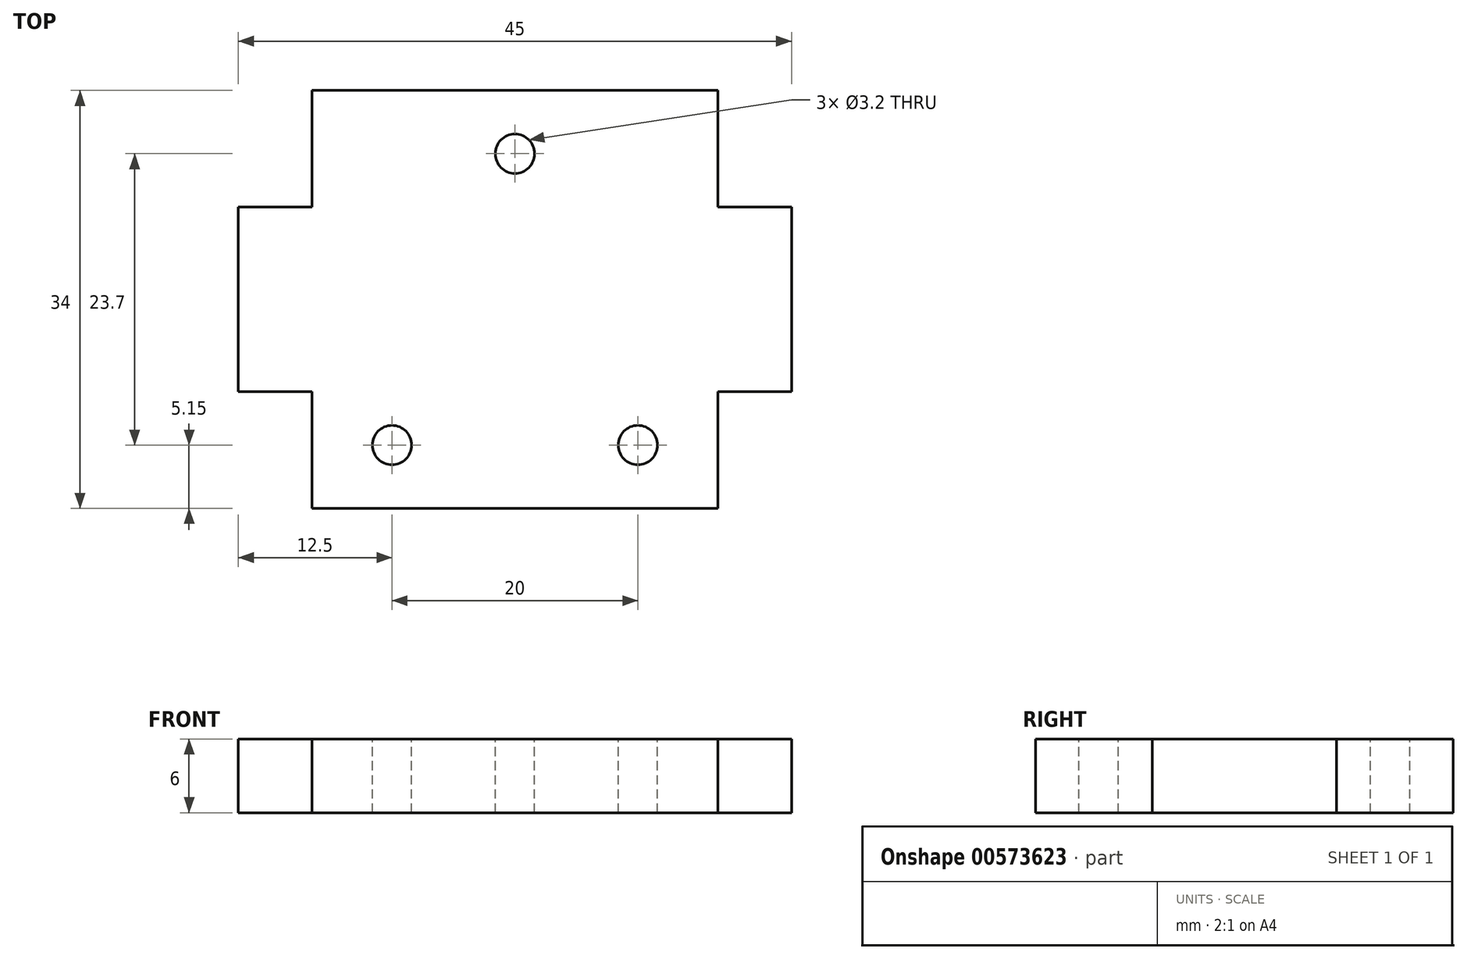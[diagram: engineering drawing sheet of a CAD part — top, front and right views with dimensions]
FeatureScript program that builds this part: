
annotation { "Feature Type Name" : "Feature", "Feature Type Description" : "" }
export const myFeature = defineFeature(function(context is Context, id is Id, definition is map)
    precondition{}
    {
        {
            var Q0;
            Q0=qCreatedBy(makeId("Top.planeOp"),FACE);
            var sketch = newSketch(context, id + "F0", { "sketchPlane" : qUnion([Q0])});
            skLineSegment(sketch, "E0.bottom", {"start": v(16.5, -17) * mm, "end": v(-16.5, -17) * mm});
            skLineSegment(sketch, "E0.top", {"start": v(16.5, 17) * mm, "end": v(-16.5, 17) * mm});
            skLineSegment(sketch, "E0.left", {"start": v(16.5, -17) * mm, "end": v(16.5, 17) * mm});
            skLineSegment(sketch, "E0.right", {"start": v(-16.5, -17) * mm, "end": v(-16.5, 17) * mm});
            skPoint(sketch, "E0.middle", {"position": v(0, 0) * mm});
            skSolve(sketch);
        }
        {
            var Q0;
            Q0 = qSketchRegion(id + "F0", true);
            extrude(context, id + "F1", {"entities" : qUnion([Q0]), "depth" : 6 * mm, "offsetDistance" : 25 * mm});
        }
        {
            var Q0;
            Q0=makeQuery(id+"F4.boolean.opBoolean","MERGE",FACE,{"derivedFrom":[makeQuery(id+"F1.opExtrude","CAP_FACE",FACE,{"disambiguationData":[OSD([sQuery(id+"F0.wireOp",EDGE,"E0.bottom"),sQuery(id+"F0.wireOp",EDGE,"E0.top"),sQuery(id+"F0.wireOp",EDGE,"E0.left"),sQuery(id+"F0.wireOp",EDGE,"E0.right")])],"isStart":false}),makeQuery(id+"F4.opExtrude","CAP_FACE",FACE,{"disambiguationData":[OSD([sQuery(id+"F3.wireOp",EDGE,"E9.bottom"),sQuery(id+"F3.wireOp",EDGE,"E9.top"),sQuery(id+"F3.wireOp",EDGE,"E9.left"),sQuery(id+"F3.wireOp",EDGE,"E9.right")])],"isStart":false}),makeQuery(id+"F4.opExtrude","CAP_FACE",FACE,{"disambiguationData":[OSD([sQuery(id+"F3.wireOp",EDGE,"E11.MirrorCS"),sQuery(id+"F3.wireOp",EDGE,"E12.MirrorCS"),sQuery(id+"F3.wireOp",EDGE,"E13.MirrorCS"),sQuery(id+"F3.wireOp",EDGE,"E14.MirrorCS")])],"isStart":false})]});
            var sketch = newSketch(context, id + "F2", { "sketchPlane" : qUnion([Q0])});
            skCircle(sketch, "E1", {"center": v(-10, -11.85) * mm, "radius": 1.6 * mm});
            skCircle(sketch, "E2", {"center": v(10, -11.85) * mm, "radius": 1.6 * mm});
            skCircle(sketch, "E3", {"center": v(0, 11.85) * mm, "radius": 1.6 * mm});
            skLineSegment(sketch, "E4", {"start": v(-10, -11.85) * mm, "end": v(10, -11.85) * mm, "construction": true});
            skPoint(sketch, "E5", {"position": v(0, -11.85) * mm});
            skLineSegment(sketch, "E6", {"start": v(0, -11.85) * mm, "end": v(0, 11.85) * mm, "construction": true});
            skPoint(sketch, "E7", {"position": v(0, 0) * mm});
            skSolve(sketch);
        }
        {
            var Q0;
            Q0=qCreatedBy(makeId("Top.planeOp"),FACE);
            var sketch = newSketch(context, id + "F3", { "sketchPlane" : qUnion([Q0])});
            skLineSegment(sketch, "E8", {"start": v(0, 17) * mm, "end": v(0, -17) * mm, "construction": true});
            skLineSegment(sketch, "E9.bottom", {"start": v(-16.5, 7.5) * mm, "end": v(-22.5, 7.5) * mm});
            skLineSegment(sketch, "E9.top", {"start": v(-16.5, -7.5) * mm, "end": v(-22.5, -7.5) * mm});
            skLineSegment(sketch, "E9.left", {"start": v(-16.5, 7.5) * mm, "end": v(-16.5, -7.5) * mm});
            skLineSegment(sketch, "E9.right", {"start": v(-22.5, 7.5) * mm, "end": v(-22.5, -7.5) * mm});
            skLineSegment(sketch, "E10", {"start": v(-22.5, 0) * mm, "end": v(0, 0) * mm, "construction": true});
            skLineSegment(sketch, "E11.MirrorCS", {"start": v(22.5, 7.5) * mm, "end": v(22.5, -7.5) * mm});
            skLineSegment(sketch, "E12.MirrorCS", {"start": v(16.5, 7.5) * mm, "end": v(16.5, -7.5) * mm});
            skLineSegment(sketch, "E13.MirrorCS", {"start": v(16.5, 7.5) * mm, "end": v(22.5, 7.5) * mm});
            skLineSegment(sketch, "E14.MirrorCS", {"start": v(16.5, -7.5) * mm, "end": v(22.5, -7.5) * mm});
            skSolve(sketch);
        }
        {
            var Q0;
            Q0 = qSketchRegion(id + "F3", true);
            extrude(context, id + "F4", {"entities" : qUnion([Q0]), "operationType" : NewBodyOperationType.ADD, "depth" : 6 * mm, "offsetDistance" : 25 * mm});
        }
        {
            var Q0;
            Q0 = qSketchRegion(id + "F2", true);
            var Q1;
            Q1=makeQuery(id+"F4.boolean.opBoolean","MERGE",FACE,{"derivedFrom":[makeQuery(id+"F1.opExtrude","CAP_FACE",FACE,{"disambiguationData":[OSD([sQuery(id+"F0.wireOp",EDGE,"E0.bottom"),sQuery(id+"F0.wireOp",EDGE,"E0.top"),sQuery(id+"F0.wireOp",EDGE,"E0.left"),sQuery(id+"F0.wireOp",EDGE,"E0.right")])],"isStart":true}),makeQuery(id+"F4.opExtrude","CAP_FACE",FACE,{"disambiguationData":[OSD([sQuery(id+"F3.wireOp",EDGE,"E9.bottom"),sQuery(id+"F3.wireOp",EDGE,"E9.top"),sQuery(id+"F3.wireOp",EDGE,"E9.left"),sQuery(id+"F3.wireOp",EDGE,"E9.right")])],"isStart":true}),makeQuery(id+"F4.opExtrude","CAP_FACE",FACE,{"disambiguationData":[OSD([sQuery(id+"F3.wireOp",EDGE,"E11.MirrorCS"),sQuery(id+"F3.wireOp",EDGE,"E12.MirrorCS"),sQuery(id+"F3.wireOp",EDGE,"E13.MirrorCS"),sQuery(id+"F3.wireOp",EDGE,"E14.MirrorCS")])],"isStart":true})]});
            extrude(context, id + "F5", {"entities" : qUnion([Q0]), "operationType" : NewBodyOperationType.REMOVE, "endBound" : BoundingType.UP_TO_SURFACE, "oppositeDirection" : true, "depth" : 25 * mm, "endBoundEntityFace" : qUnion([Q1]), "offsetDistance" : 25 * mm});
        }
    });
